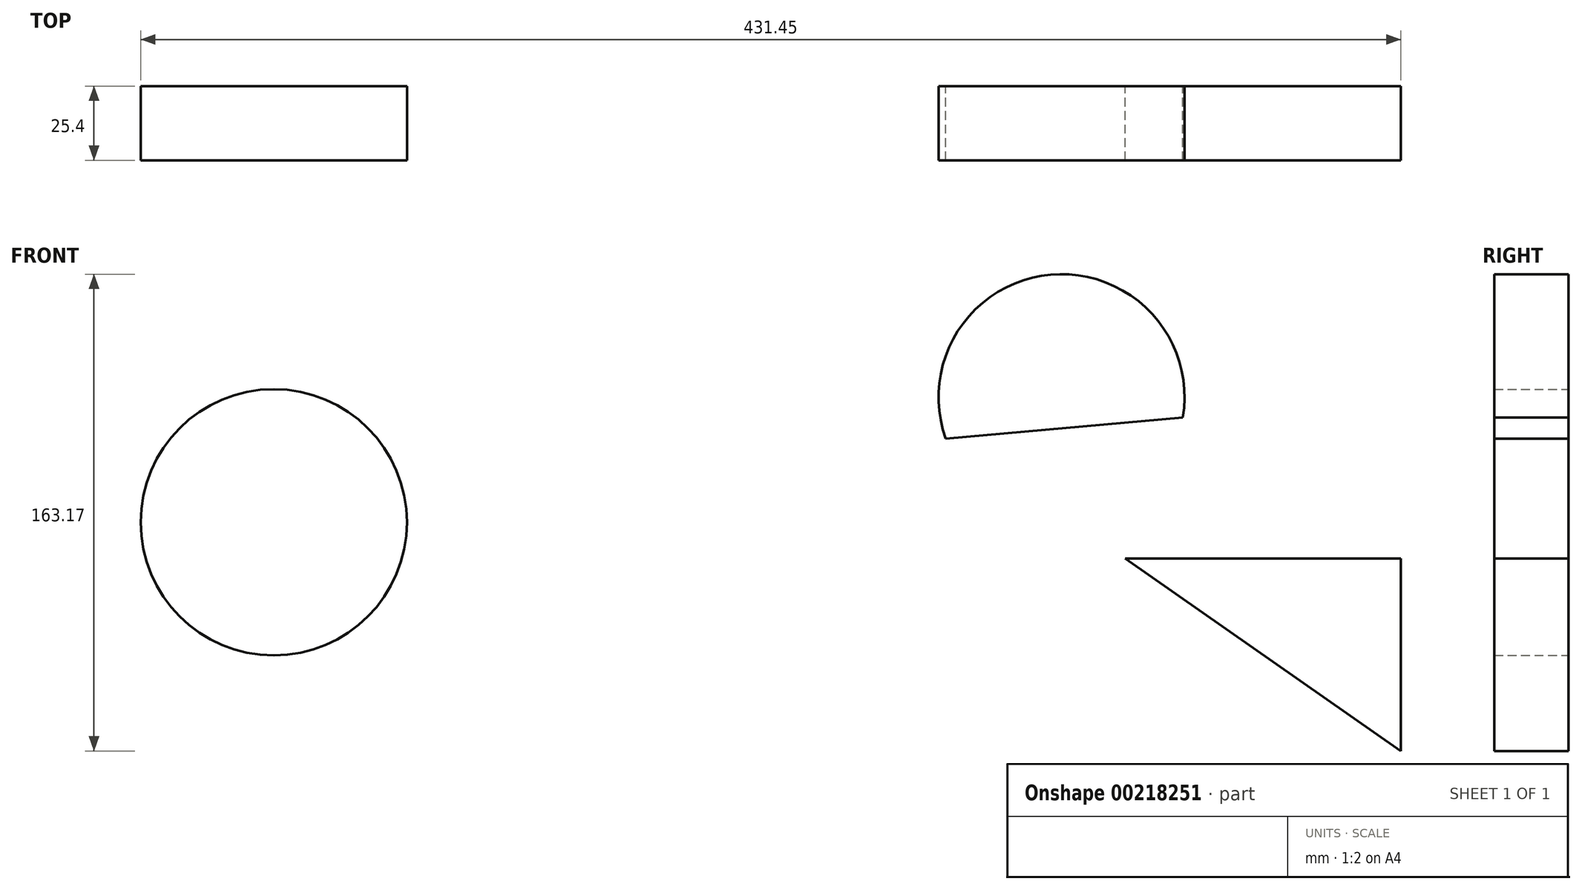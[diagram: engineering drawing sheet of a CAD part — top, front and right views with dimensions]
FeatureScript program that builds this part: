
annotation { "Feature Type Name" : "Feature", "Feature Type Description" : "" }
export const myFeature = defineFeature(function(context is Context, id is Id, definition is map)
    precondition{}
    {
        {
            var Q0;
            Q0=qCreatedBy(makeId("Front.planeOp"),FACE);
            var sketch = newSketch(context, id + "F0", { "sketchPlane" : qUnion([Q0])});
            skCircle(sketch, "E0", {"center": v(-167.7, 19.63) * mm, "radius": 45.58 * mm});
            skCircle(sketch, "E1", {"center": v(-87.36, -90.63) * mm, "radius": 106.4 * mm});
            skArc(sketch, "E2", {"start": v(143.55, 55.49) * mm, "mid": v(98.29, 104.39) * mm, "end": v(62.34, 48.29) * mm});
            skLineSegment(sketch, "E3", {"start": v(62.34, 48.29) * mm, "end": v(143.55, 55.49) * mm});
            skLineSegment(sketch, "E4.bottom", {"start": v(123.8, 7.2) * mm, "end": v(218.18, 7.2) * mm});
            skLineSegment(sketch, "E4.top", {"start": v(123.8, -58.62) * mm, "end": v(218.18, -58.62) * mm});
            skLineSegment(sketch, "E4.left", {"start": v(123.8, 7.2) * mm, "end": v(123.8, -58.62) * mm});
            skLineSegment(sketch, "E4.right", {"start": v(218.18, 7.2) * mm, "end": v(218.18, -58.62) * mm});
            skLineSegment(sketch, "E5", {"start": v(123.8, 7.2) * mm, "end": v(218.18, -58.62) * mm});
            skSolve(sketch);
        }
        {
            var Q0;
            {var subQ0=sQuery(id+"F0.wireOp",EDGE,"E1");var subQ1=sQuery(id+"F0.wireOp",EDGE,"E0");var subQ2=makeQuery(id+"F0.imprint","INTERSECT",VERTEX,{"disambiguationData":[OD(0.0)],"derivedFrom":[subQ1,subQ0]});Q0=makeQuery(id+"F0.imprint","IMPRINT",FACE,{"disambiguationData":[TD([[makeQuery(id+"F0.imprint","IMPRINT",EDGE,{"disambiguationData":[TD([[subQ2,-1.0]])],"derivedFrom":subQ1}),1.0]])]});}
            var Q1;
            {var subQ0=sQuery(id+"F0.wireOp",EDGE,"E1");var subQ1=sQuery(id+"F0.wireOp",EDGE,"E0");var subQ2=makeQuery(id+"F0.imprint","INTERSECT",VERTEX,{"disambiguationData":[OD(0.0)],"derivedFrom":[subQ1,subQ0]});Q1=makeQuery(id+"F0.imprint","IMPRINT",FACE,{"disambiguationData":[TD([[makeQuery(id+"F0.imprint","IMPRINT",EDGE,{"disambiguationData":[TD([[subQ2,1.0]])],"derivedFrom":subQ1}),1.0]])]});}
            var Q2;
            Q2=makeQuery(id+"F0.imprint","IMPRINT",FACE,{"disambiguationData":[TD([[makeQuery(id+"F0.imprint","IMPRINT",EDGE,{"derivedFrom":sQuery(id+"F0.wireOp",EDGE,"E2")}),1.0]])]});
            var Q3;
            Q3=makeQuery(id+"F0.imprint","IMPRINT",FACE,{"disambiguationData":[TD([[makeQuery(id+"F0.imprint","IMPRINT",EDGE,{"derivedFrom":sQuery(id+"F0.wireOp",EDGE,"E4.bottom")}),-1.0]])]});
            extrude(context, id + "F1", {"entities" : qUnion([Q0, Q1, Q2, Q3]), "depth" : 25.4 * mm});
        }
    });
